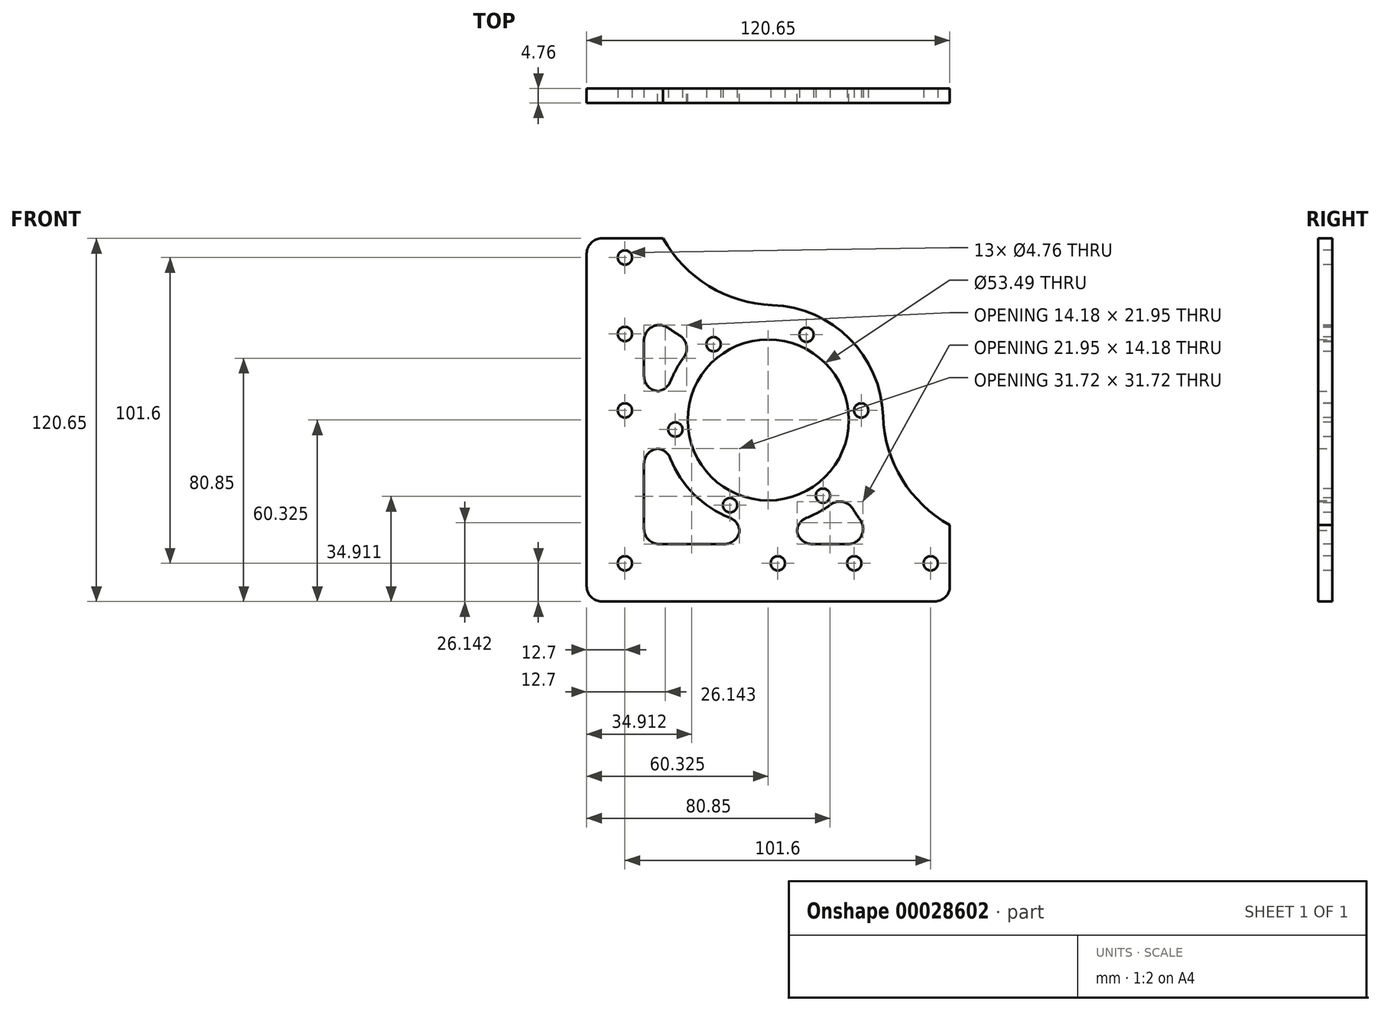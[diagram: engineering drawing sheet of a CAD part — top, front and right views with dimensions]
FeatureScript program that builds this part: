
annotation { "Feature Type Name" : "Feature", "Feature Type Description" : "" }
export const myFeature = defineFeature(function(context is Context, id is Id, definition is map)
    precondition{}
    {
        {
            var Q0;
            Q0=qCreatedBy(makeId("Front.planeOp"),FACE);
            var sketch = newSketch(context, id + "F0", { "sketchPlane" : qUnion([Q0])});
            skLineSegment(sketch, "E0.bottom", {"start": v(1.11, 0) * mm, "end": v(121.76, 0) * mm});
            skLineSegment(sketch, "E0.top", {"start": v(1.11, 120.65) * mm, "end": v(26.51, 120.65) * mm});
            skLineSegment(sketch, "E0.left", {"start": v(1.11, 0) * mm, "end": v(1.11, 120.65) * mm});
            skLineSegment(sketch, "E0.right", {"start": v(121.76, 0) * mm, "end": v(121.76, 25.4) * mm});
            skCircle(sketch, "E1", {"center": v(61.44, 60.33) * mm, "radius": 26.75 * mm});
            skArc(sketch, "E2", {"start": v(99.6, 61.61) * mm, "mid": v(88.43, 87.32) * mm, "end": v(62.72, 98.48) * mm});
            skArc(sketch, "E3", {"start": v(26.51, 120.65) * mm, "mid": v(41.7, 104.79) * mm, "end": v(62.72, 98.48) * mm});
            skArc(sketch, "E4", {"start": v(99.6, 61.61) * mm, "mid": v(105.9, 40.58) * mm, "end": v(121.76, 25.4) * mm});
            skSolve(sketch);
        }
        {
            var Q0;
            Q0=makeQuery(id+"F0.imprint","IMPRINT",FACE,{"disambiguationData":[TD([[makeQuery(id+"F0.imprint","IMPRINT",EDGE,{"derivedFrom":sQuery(id+"F0.wireOp",EDGE,"E0.bottom")}),1.0]])]});
            extrude(context, id + "F1", {"entities" : qUnion([Q0]), "depth" : 4.76 * mm});
        }
        {
            var Q0;
            Q0=makeQuery(id+"F1.opExtrude","CAP_FACE",FACE,{"disambiguationData":[OSD([sQuery(id+"F0.wireOp",EDGE,"E0.bottom"),sQuery(id+"F0.wireOp",EDGE,"E0.top"),sQuery(id+"F0.wireOp",EDGE,"E0.left"),sQuery(id+"F0.wireOp",EDGE,"E0.right"),sQuery(id+"F0.wireOp",EDGE,"E1"),sQuery(id+"F0.wireOp",EDGE,"E2"),sQuery(id+"F0.wireOp",EDGE,"E3"),sQuery(id+"F0.wireOp",EDGE,"E4")])],"isStart":false});
            var sketch = newSketch(context, id + "F2", { "sketchPlane" : qUnion([Q0])});
            skArc(sketch, "E5", {"start": v(37.27, 85.54) * mm, "mid": v(31.5, 78.32) * mm, "end": v(27.83, 69.85) * mm});
            skLineSegment(sketch, "E6", {"start": v(20.16, 97.7) * mm, "end": v(20.16, 69.85) * mm});
            skLineSegment(sketch, "E7", {"start": v(20.16, 69.85) * mm, "end": v(27.83, 69.85) * mm});
            skLineSegment(sketch, "E8", {"start": v(20.16, 50.8) * mm, "end": v(20.16, 19.05) * mm});
            skLineSegment(sketch, "E9", {"start": v(20.16, 19.05) * mm, "end": v(51.91, 19.05) * mm});
            skLineSegment(sketch, "E10", {"start": v(51.91, 19.05) * mm, "end": v(51.91, 26.72) * mm});
            skLineSegment(sketch, "E11", {"start": v(27.83, 50.8) * mm, "end": v(20.16, 50.8) * mm});
            skLineSegment(sketch, "E12", {"start": v(70.96, 19.05) * mm, "end": v(98.8, 19.05) * mm});
            skLineSegment(sketch, "E13", {"start": v(70.96, 26.72) * mm, "end": v(70.96, 19.05) * mm});
            skLineSegment(sketch, "E14", {"start": v(2.96, 60.33) * mm, "end": v(61.44, 60.33) * mm, "construction": true});
            skLineSegment(sketch, "E15", {"start": v(61.44, 60.32) * mm, "end": v(61.44, 13.04) * mm, "construction": true});
            skArc(sketch, "E16.0", {"start": v(86.65, 36.16) * mm, "mid": v(92, 27.09) * mm, "end": v(98.8, 19.05) * mm});
            skArc(sketch, "E17.trimOffspring", {"start": v(70.96, 26.72) * mm, "mid": v(79.43, 30.4) * mm, "end": v(86.65, 36.16) * mm});
            skArc(sketch, "E18.trimOffspring", {"start": v(27.83, 50.8) * mm, "mid": v(36.74, 35.63) * mm, "end": v(51.91, 26.72) * mm});
            skArc(sketch, "E19.0", {"start": v(20.16, 97.7) * mm, "mid": v(28.2, 90.89) * mm, "end": v(37.27, 85.54) * mm});
            skSolve(sketch);
        }
        {
            var Q0;
            Q0=makeQuery(id+"F2.imprint","IMPRINT",FACE,{"disambiguationData":[TD([[makeQuery(id+"F2.imprint","IMPRINT",EDGE,{"derivedFrom":sQuery(id+"F2.wireOp",EDGE,"E5")}),-1.0]])]});
            var Q1;
            Q1=makeQuery(id+"F2.imprint","IMPRINT",FACE,{"disambiguationData":[TD([[makeQuery(id+"F2.imprint","IMPRINT",EDGE,{"derivedFrom":sQuery(id+"F2.wireOp",EDGE,"E12")}),1.0]])]});
            var Q2;
            Q2=makeQuery(id+"F2.imprint","IMPRINT",FACE,{"disambiguationData":[TD([[makeQuery(id+"F2.imprint","IMPRINT",EDGE,{"derivedFrom":sQuery(id+"F2.wireOp",EDGE,"E8")}),1.0]])]});
            extrude(context, id + "F3", {"entities" : qUnion([Q0, Q1, Q2]), "operationType" : NewBodyOperationType.REMOVE, "endBound" : BoundingType.THROUGH_ALL, "oppositeDirection" : true, "depth" : 25.4 * mm});
        }
        {
            var Q0;
            Q0=makeQuery(id+"F1.opExtrude","CAP_FACE",FACE,{"disambiguationData":[OSD([sQuery(id+"F0.wireOp",EDGE,"E0.bottom"),sQuery(id+"F0.wireOp",EDGE,"E0.top"),sQuery(id+"F0.wireOp",EDGE,"E0.left"),sQuery(id+"F0.wireOp",EDGE,"E0.right"),sQuery(id+"F0.wireOp",EDGE,"E1"),sQuery(id+"F0.wireOp",EDGE,"E2"),sQuery(id+"F0.wireOp",EDGE,"E3"),sQuery(id+"F0.wireOp",EDGE,"E4")])],"isStart":false});
            var sketch = newSketch(context, id + "F4", { "sketchPlane" : qUnion([Q0])});
            skLineSegment(sketch, "E20", {"start": v(13.81, 114.3) * mm, "end": v(13.81, 12.7) * mm});
            skLineSegment(sketch, "E21", {"start": v(13.81, 12.7) * mm, "end": v(115.41, 12.7) * mm});
            skPoint(sketch, "E22", {"position": v(13.81, 88.9) * mm});
            skPoint(sketch, "E23", {"position": v(13.81, 63.5) * mm});
            skPoint(sketch, "E24", {"position": v(90.01, 12.7) * mm});
            skPoint(sketch, "E25", {"position": v(64.61, 12.7) * mm});
            skCircle(sketch, "E26.cCircle", {"center": v(61.44, 60.33) * mm, "radius": 31.04 * mm, "construction": true});
            skLineSegment(sketch, "E26.0", {"start": v(92.31, 63.48) * mm, "end": v(79.6, 35.17) * mm});
            skLineSegment(sketch, "E26.1", {"start": v(79.6, 35.17) * mm, "end": v(48.73, 32) * mm});
            skLineSegment(sketch, "E26.2", {"start": v(48.73, 32) * mm, "end": v(30.56, 57.17) * mm});
            skLineSegment(sketch, "E26.3", {"start": v(30.56, 57.17) * mm, "end": v(43.26, 85.48) * mm});
            skLineSegment(sketch, "E26.4", {"start": v(43.26, 85.48) * mm, "end": v(74.14, 88.64) * mm});
            skLineSegment(sketch, "E26.5", {"start": v(74.14, 88.64) * mm, "end": v(92.31, 63.48) * mm});
            skSolve(sketch);
        }
        {
            var Q0;
            Q0=sQuery(id+"F4.wireOp",VERTEX,"E20.start");
            var Q1;
            Q1=sQuery(id+"F4.wireOp",VERTEX,"E22");
            var Q2;
            Q2=sQuery(id+"F4.wireOp",VERTEX,"E23");
            var Q3;
            Q3=sQuery(id+"F4.wireOp",VERTEX,"E21.start");
            var Q4;
            Q4=sQuery(id+"F4.wireOp",VERTEX,"E25");
            var Q5;
            Q5=sQuery(id+"F4.wireOp",VERTEX,"E24");
            var Q6;
            Q6=sQuery(id+"F4.wireOp",VERTEX,"E21.end");
            var Q7;
            Q7=sQuery(id+"F4.wireOp",VERTEX,"E26.5.start");
            var Q8;
            Q8=sQuery(id+"F4.wireOp",VERTEX,"E26.0.start");
            var Q9;
            Q9=sQuery(id+"F4.wireOp",VERTEX,"E26.1.start");
            var Q10;
            Q10=sQuery(id+"F4.wireOp",VERTEX,"E26.2.start");
            var Q11;
            Q11=sQuery(id+"F4.wireOp",VERTEX,"E26.3.start");
            var Q12;
            Q12=sQuery(id+"F4.wireOp",VERTEX,"E26.4.start");
            var Q13;
            Q13=makeQuery(id+"F1.opExtrude","SWEPT_BODY",BODY,{"disambiguationData":[OSD([sQuery(id+"F0.wireOp",EDGE,"E0.bottom"),sQuery(id+"F0.wireOp",EDGE,"E0.top"),sQuery(id+"F0.wireOp",EDGE,"E0.left"),sQuery(id+"F0.wireOp",EDGE,"E0.right"),sQuery(id+"F0.wireOp",EDGE,"E1"),sQuery(id+"F0.wireOp",EDGE,"E2"),sQuery(id+"F0.wireOp",EDGE,"E3"),sQuery(id+"F0.wireOp",EDGE,"E4")])]});
            hole(context, id + "F5", {"style" : HoleStyle.SIMPLE, "holeDiameter" : 4.76 * mm, "endStyle" : HoleEndStyle.THROUGH, "locations" : qUnion([Q0, Q1, Q2, Q3, Q4, Q5, Q6, Q7, Q8, Q9, Q10, Q11, Q12]), "scope" : qUnion([Q13])});
        }
        {
            var Q0;
            Q0=makeQuery(id+"F3.boolean.opBoolean","COPY",EDGE,{"derivedFrom":makeQuery(id+"F3.opExtrude","SWEPT_EDGE",EDGE,{"disambiguationData":[OSD([sQuery(id+"F2.wireOp",EDGE,"E6"),sQuery(id+"F2.wireOp",EDGE,"E7")])]})});
            var Q1;
            Q1=makeQuery(id+"F3.boolean.opBoolean","COPY",EDGE,{"derivedFrom":makeQuery(id+"F3.opExtrude","SWEPT_EDGE",EDGE,{"disambiguationData":[OSD([sQuery(id+"F2.wireOp",EDGE,"E6"),sQuery(id+"F2.wireOp",EDGE,"E19.0")])]})});
            var Q2;
            Q2=makeQuery(id+"F3.boolean.opBoolean","COPY",EDGE,{"derivedFrom":makeQuery(id+"F3.opExtrude","SWEPT_EDGE",EDGE,{"disambiguationData":[OSD([sQuery(id+"F2.wireOp",EDGE,"E5"),sQuery(id+"F2.wireOp",EDGE,"E19.0")])]})});
            var Q3;
            Q3=makeQuery(id+"F3.boolean.opBoolean","COPY",EDGE,{"derivedFrom":makeQuery(id+"F3.opExtrude","SWEPT_EDGE",EDGE,{"disambiguationData":[OSD([sQuery(id+"F2.wireOp",EDGE,"E5"),sQuery(id+"F2.wireOp",EDGE,"E7")])]})});
            var Q4;
            Q4=makeQuery(id+"F3.boolean.opBoolean","COPY",EDGE,{"derivedFrom":makeQuery(id+"F3.opExtrude","SWEPT_EDGE",EDGE,{"disambiguationData":[OSD([sQuery(id+"F2.wireOp",EDGE,"E8"),sQuery(id+"F2.wireOp",EDGE,"E11")])]})});
            var Q5;
            Q5=makeQuery(id+"F3.boolean.opBoolean","COPY",EDGE,{"derivedFrom":makeQuery(id+"F3.opExtrude","SWEPT_EDGE",EDGE,{"disambiguationData":[OSD([sQuery(id+"F2.wireOp",EDGE,"E16.0"),sQuery(id+"F2.wireOp",EDGE,"E17.trimOffspring")])]})});
            var Q6;
            Q6=makeQuery(id+"F3.boolean.opBoolean","COPY",EDGE,{"derivedFrom":makeQuery(id+"F3.opExtrude","SWEPT_EDGE",EDGE,{"disambiguationData":[OSD([sQuery(id+"F2.wireOp",EDGE,"E11"),sQuery(id+"F2.wireOp",EDGE,"E18.trimOffspring")])]})});
            var Q7;
            Q7=makeQuery(id+"F3.boolean.opBoolean","COPY",EDGE,{"derivedFrom":makeQuery(id+"F3.opExtrude","SWEPT_EDGE",EDGE,{"disambiguationData":[OSD([sQuery(id+"F2.wireOp",EDGE,"E12"),sQuery(id+"F2.wireOp",EDGE,"E13")])]})});
            var Q8;
            Q8=makeQuery(id+"F3.boolean.opBoolean","COPY",EDGE,{"derivedFrom":makeQuery(id+"F3.opExtrude","SWEPT_EDGE",EDGE,{"disambiguationData":[OSD([sQuery(id+"F2.wireOp",EDGE,"E8"),sQuery(id+"F2.wireOp",EDGE,"E9")])]})});
            var Q9;
            Q9=makeQuery(id+"F3.boolean.opBoolean","COPY",EDGE,{"derivedFrom":makeQuery(id+"F3.opExtrude","SWEPT_EDGE",EDGE,{"disambiguationData":[OSD([sQuery(id+"F2.wireOp",EDGE,"E9"),sQuery(id+"F2.wireOp",EDGE,"E10")])]})});
            var Q10;
            Q10=makeQuery(id+"F3.boolean.opBoolean","COPY",EDGE,{"derivedFrom":makeQuery(id+"F3.opExtrude","SWEPT_EDGE",EDGE,{"disambiguationData":[OSD([sQuery(id+"F2.wireOp",EDGE,"E12"),sQuery(id+"F2.wireOp",EDGE,"E16.0")])]})});
            var Q11;
            Q11=makeQuery(id+"F3.boolean.opBoolean","COPY",EDGE,{"derivedFrom":makeQuery(id+"F3.opExtrude","SWEPT_EDGE",EDGE,{"disambiguationData":[OSD([sQuery(id+"F2.wireOp",EDGE,"E10"),sQuery(id+"F2.wireOp",EDGE,"E18.trimOffspring")])]})});
            var Q12;
            Q12=makeQuery(id+"F3.boolean.opBoolean","COPY",EDGE,{"derivedFrom":makeQuery(id+"F3.opExtrude","SWEPT_EDGE",EDGE,{"disambiguationData":[OSD([sQuery(id+"F2.wireOp",EDGE,"E13"),sQuery(id+"F2.wireOp",EDGE,"E17.trimOffspring")])]})});
            var Q13;
            Q13=makeQuery(id+"F1.opExtrude","SWEPT_EDGE",EDGE,{"disambiguationData":[OSD([sQuery(id+"F0.wireOp",EDGE,"E0.top"),sQuery(id+"F0.wireOp",EDGE,"E0.left")])]});
            var Q14;
            Q14=makeQuery(id+"F1.opExtrude","SWEPT_EDGE",EDGE,{"disambiguationData":[OSD([sQuery(id+"F0.wireOp",EDGE,"E0.bottom"),sQuery(id+"F0.wireOp",EDGE,"E0.left")])]});
            var Q15;
            Q15=makeQuery(id+"F1.opExtrude","SWEPT_EDGE",EDGE,{"disambiguationData":[OSD([sQuery(id+"F0.wireOp",EDGE,"E0.bottom"),sQuery(id+"F0.wireOp",EDGE,"E0.right")])]});
            fillet(context, id + "F6", {"entities" : qUnion([Q0, Q1, Q2, Q3, Q4, Q5, Q6, Q7, Q8, Q9, Q10, Q11, Q12, Q13, Q14, Q15]), "radius" : 5.08 * mm, "tangentPropagation" : true, "allowEdgeOverflow" : false});
        }
    });
